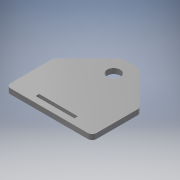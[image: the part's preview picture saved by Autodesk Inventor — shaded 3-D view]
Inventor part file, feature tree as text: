
AUTODESK INVENTOR PART (.ipt)
format: ipt  version: 2017 (Build 210142000, 142)  size: 144,896 bytes
history: native  units: mm
features: sketch x2, other x2, sheet_metal_op x1, hole x1, chamfer x1, plane x1
ambient origin geometry x8: Origin, YZ Plane, XZ Plane, XY Plane, X Axis, Y Axis, Z Axis, Center Point
bodies: Solid1 (feature_tree)
feature tree (8):
  sheet_metal_op  "Face1"
  hole  "Hole1"  [1 undecoded]
  chamfer  "Corner Round1"
  plane  "Work Plane1"
  sketch  "Sketch1"  dims[d2=95.0mm d3=100.0mm]
  other  "Plate1"
  sketch  "Sketch2"  dims[d4=40.0mm d5=40.0mm d6=40.0mm d7=40.0mm d8=0.001mm d9=20.0mm d10=50.0mm d11=15.0mm d12=6.0mm d13=4.0mm d14=2.0mm d15=90.0deg d16=6.0mm d17=20.594885mm d18=5.0mm d19=4.0mm d20=45.0mm d21=7.0mm d22=22.5mm d23=6.0mm d24=0.0mm]
  other  "Cut1"
note: 1 required parameter value undecoded (feature->parameter linkage not recoverable at this tier; creation-order binding heuristic only, values carry confidence <= 0.55)
